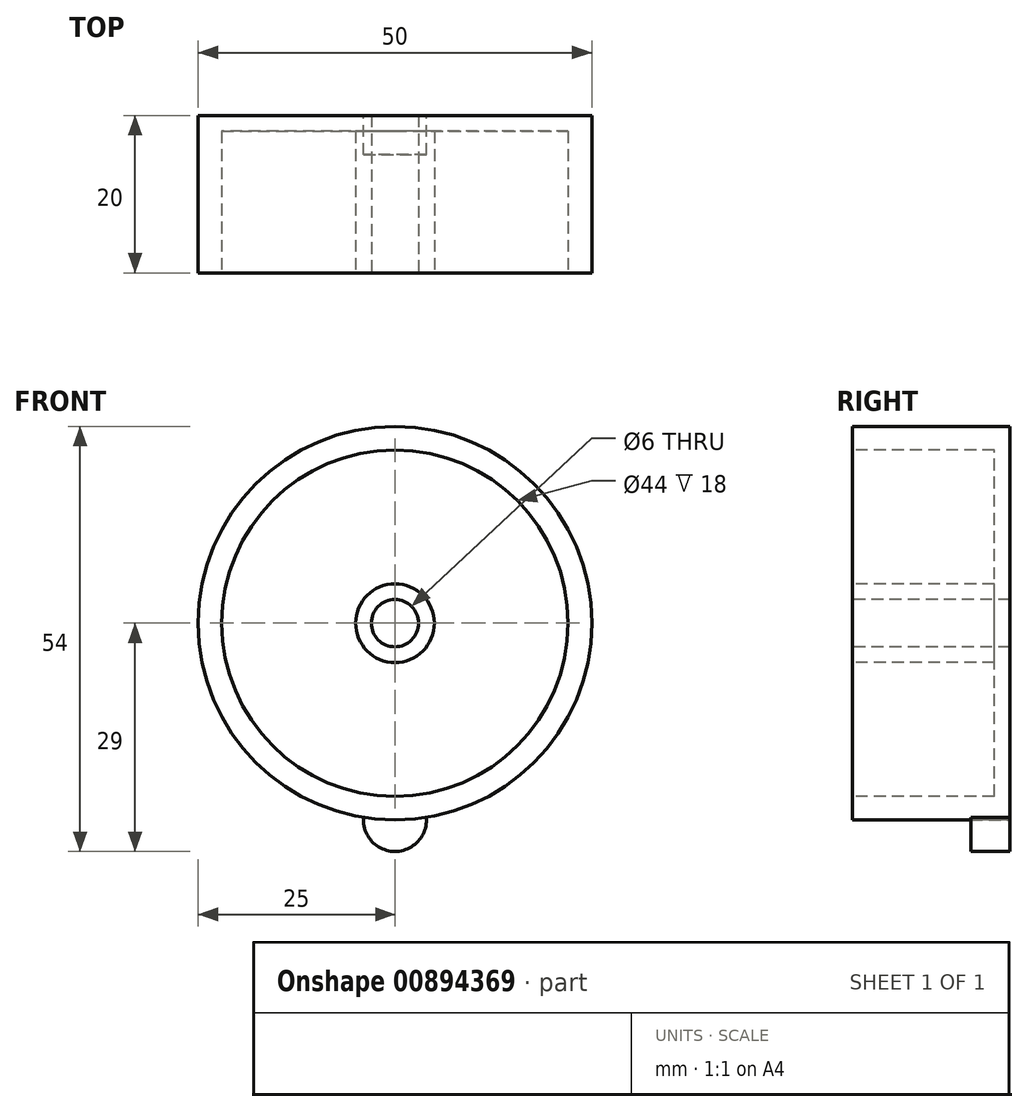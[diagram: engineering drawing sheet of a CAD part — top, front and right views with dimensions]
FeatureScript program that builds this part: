
annotation { "Feature Type Name" : "Feature", "Feature Type Description" : "" }
export const myFeature = defineFeature(function(context is Context, id is Id, definition is map)
    precondition{}
    {
        {
            var Q0;
            Q0=qCreatedBy(makeId("Front.planeOp"),FACE);
            var sketch = newSketch(context, id + "F0", { "sketchPlane" : qUnion([Q0])});
            skCircle(sketch, "E0", {"center": v(0, 0) * mm, "radius": 25 * mm});
            skCircle(sketch, "E1", {"center": v(0, 0) * mm, "radius": 22 * mm});
            skCircle(sketch, "E2", {"center": v(0, 0) * mm, "radius": 5 * mm});
            skCircle(sketch, "E3", {"center": v(0, 0) * mm, "radius": 3 * mm});
            skSolve(sketch);
        }
        {
            var Q0;
            Q0=makeQuery(id+"F0.imprint","IMPRINT",FACE,{"disambiguationData":[TD([[makeQuery(id+"F0.imprint","IMPRINT",EDGE,{"derivedFrom":sQuery(id+"F0.wireOp",EDGE,"E2")}),1.0]])]});
            var Q1;
            Q1=makeQuery(id+"F0.imprint","IMPRINT",FACE,{"disambiguationData":[TD([[makeQuery(id+"F0.imprint","IMPRINT",EDGE,{"derivedFrom":sQuery(id+"F0.wireOp",EDGE,"E1")}),1.0]])]});
            var Q2;
            Q2=makeQuery(id+"F0.imprint","IMPRINT",FACE,{"disambiguationData":[TD([[makeQuery(id+"F0.imprint","IMPRINT",EDGE,{"derivedFrom":sQuery(id+"F0.wireOp",EDGE,"E0")}),1.0]])]});
            extrude(context, id + "F1", {"entities" : qUnion([Q0, Q1, Q2]), "oppositeDirection" : true, "depth" : 20 * mm, "offsetDistance" : 25 * mm});
        }
        {
            var Q0;
            Q0=makeQuery(id+"F0.imprint","IMPRINT",FACE,{"disambiguationData":[TD([[makeQuery(id+"F0.imprint","IMPRINT",EDGE,{"derivedFrom":sQuery(id+"F0.wireOp",EDGE,"E1")}),1.0]])]});
            extrude(context, id + "F2", {"entities" : qUnion([Q0]), "operationType" : NewBodyOperationType.REMOVE, "oppositeDirection" : true, "depth" : 18 * mm, "offsetDistance" : 25 * mm});
        }
        {
            var Q0;
            Q0=makeQuery(id+"F1.opExtrude","CAP_FACE",FACE,{"disambiguationData":[OSD([sQuery(id+"F0.wireOp",EDGE,"E0"),sQuery(id+"F0.wireOp",EDGE,"E3")])],"isStart":false});
            var sketch = newSketch(context, id + "F3", { "sketchPlane" : qUnion([Q0])});
            skCircle(sketch, "E4", {"center": v(0, -25) * mm, "radius": 4 * mm});
            skSolve(sketch);
        }
        {
            var Q0;
            {var subQ0=sQuery(id+"F3.wireOp",EDGE,"E4");var subQ1=makeQuery(id+"F1.opExtrude","CAP_EDGE",EDGE,{"disambiguationData":[OSD([sQuery(id+"F0.wireOp",EDGE,"E0")])],"isStart":false});var subQ2=makeQuery(id+"F3.imprint","INTERSECT",VERTEX,{"disambiguationData":[OD(0.0)],"derivedFrom":[subQ1,subQ0]});Q0=makeQuery(id+"F3.imprint","IMPRINT",FACE,{"disambiguationData":[TD([[makeQuery(id+"F3.imprint","IMPRINT",EDGE,{"disambiguationData":[TD([[subQ2,1.0]])],"derivedFrom":subQ0}),1.0]])]});}
            extrude(context, id + "F4", {"entities" : qUnion([Q0]), "oppositeDirection" : true, "depth" : 5 * mm, "offsetDistance" : 25 * mm});
        }
    });
